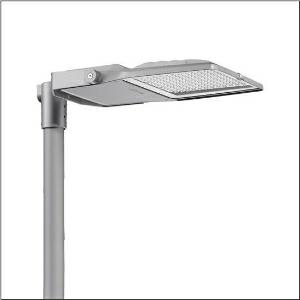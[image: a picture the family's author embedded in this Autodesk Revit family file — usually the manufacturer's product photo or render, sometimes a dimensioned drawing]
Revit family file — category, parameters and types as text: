
# Revit family: floodlight_fl_21_midi___pl61_5xa7786e4c3a_509f
name_source: partatom
category: Lighting Fixtures
units: mm (PartAtom-declared; Revit-internal decimal feet)

## family parameters
Cut with Voids When Loaded = No
Host = Face
Light Source = No
Part Type = Normal
Room Calculation Point = No
Round Connector Dimension = Use Diameter
Shared = No

## types (1)
- --- (1 x LED, 27590 lm, 212.4 W, 4000K)
    Apparent Load = 212 VA
    CIE Flux Codes = 33 65 98 100 100
    Color Rendering = 70
    Color Temperature = 4000K
    Default Elevation = 1800 mm
    Description = Floodlight FL 21 midi, floodlight, primary light control with lens, of PMMA, primary optical cover: protective disc, of toughened safety glass, transparent, light distribution: PL61, light emission: direct distribution, installation type: surface-mounted, LED, High Power LED, rated luminous flux: 27.590lm, luminous efficacy: 130lm/W, light colour: 740, colour temperature: 4000K, control gear: Smart Interface (Zhaga)D4i, control: overheat protection, constant luminous flux control, time-dependent luminous flux control, flexible luminous flux parameterisation, pre-setting: logarithmic dimming characteristic, with terminal, 6-pole, mains connection: 220..240V, AC, 50/60Hz, start of lifetime: 212W, end of service life: 231W, reduction: 95W, mast bracket, of diecast aluminium, powder-coated, Siteco® metallic grey (DB 702S), corrosivity category C5 mid according to DIN EN ISO 12944, suitable for swimming pools, chlorine-resistant, sealing non-destructively replaceable, mast bracket, of steel, galvanised, powder-coated, Siteco® metallic grey (DB 702S), Smart Interface below and above, protection rating (complete): IP66, insulation class (complete): insulation class II (safety insulation), certification: CE, ENEC, VDE, protection symbol: D, impact resistance: IK08, permissible operating ambient temperature: -40..+40°C, permissible operating ambient temperature for outdoor applications: -40..+50°C, standard: DIN EN 12944, LABS conformity tested according to VDMA 24364:2018-05, packaging unit: 1 piece

Light Distribution: PL61
    Height = 76 mm
    Lamp = 1 x LED
    Lamp Light Flux = 27590 lm
    Lamp Power = 212.4 W
    Lamp count = 1
    Length = 657 mm
    Luminous efficacy = 130 lm/W
    Manufacturer = Siteco
    ModVariant = No
    Model = 5XA7786E4C3A
    Number of Poles = 1
    OnlyDefault = Yes
    Power Factor = 1
    Product Name = Floodlight FL 21 midi | PL61
    Product group = floodlight | pylon annexe
    ProductGroupID = 6200
    Protection Class = Protection class II
    Protection Degree = IP 66
    RLX_Detail_Level = 1
    RLX_Emergency_Light_Flux = 0 lm
    RLX_Emergency_Type = 0
    RLX_Emergency_Type_DB = No
    RlxData = <blob elided: 104585 chars, md5=9e491d0b>
    Socket = socket
    Standby Power = 0 W
    System Light Flux = 27590 lm
    System Power = 212 W
    Type Comments = factory setting: luminous flux: 100 % | dim-lin: 254 | 710 mA
    Type Image = l_1007123.jpg
    URL = http://relux.com
    VarID = @adj_090432
    Voltage = 0 V
    Weight = 0.00 kg
    Width = 442 mm

## geometry (parser evidence)
native form markers: Blend x4, Sweep x11
no freeform markers — native parametric forms only
